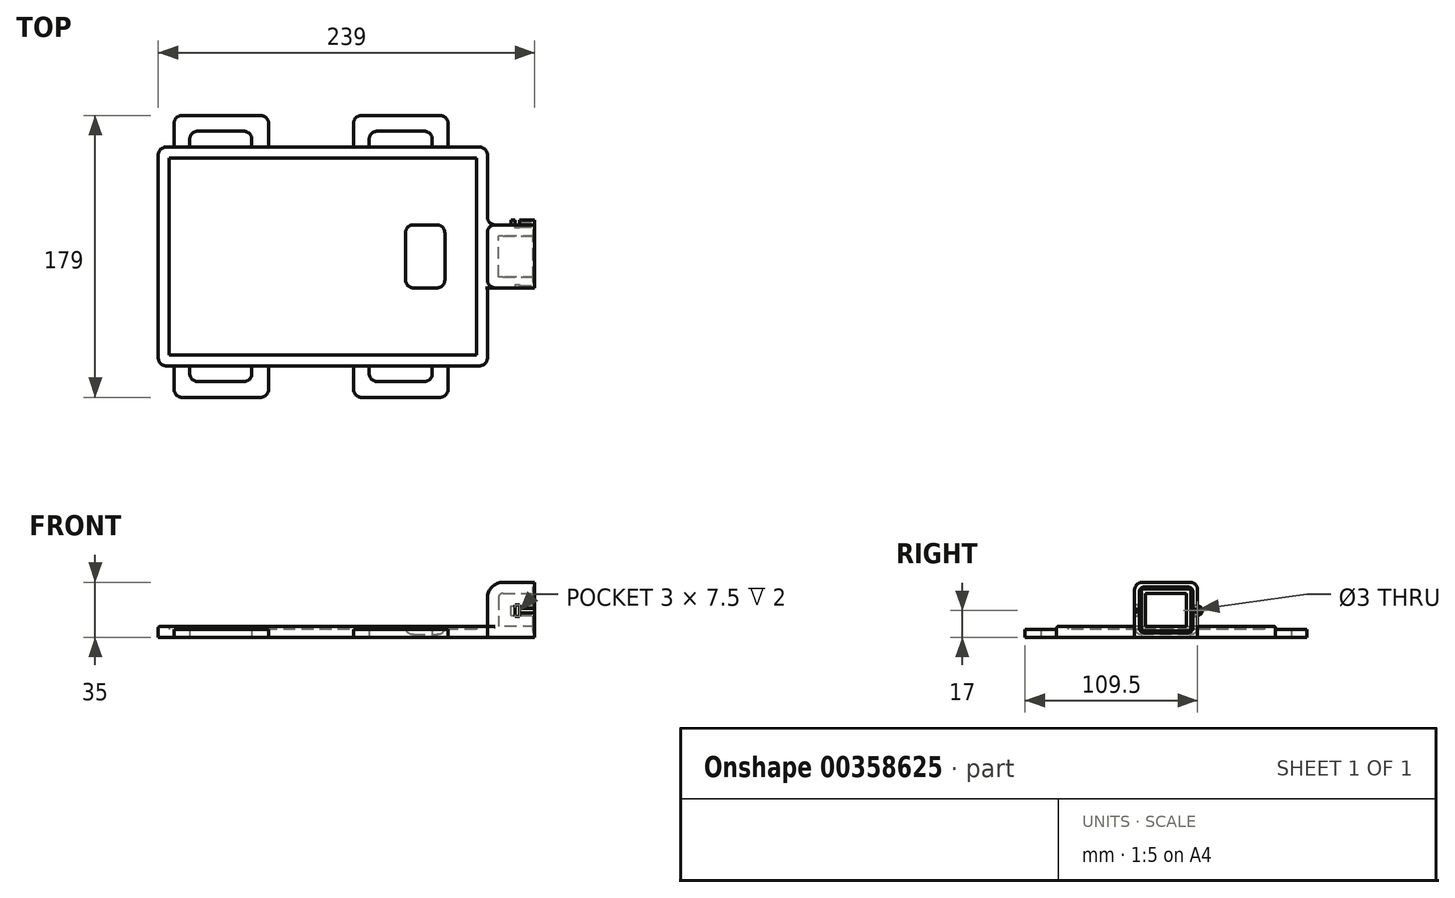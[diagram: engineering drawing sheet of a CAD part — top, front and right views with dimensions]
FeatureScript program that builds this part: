
annotation { "Feature Type Name" : "Feature", "Feature Type Description" : "" }
export const myFeature = defineFeature(function(context is Context, id is Id, definition is map)
    precondition{}
    {
        {
            var Q0;
            Q0=qCreatedBy(makeId("Top.planeOp"),FACE);
            var sketch = newSketch(context, id + "F0", { "sketchPlane" : qUnion([Q0])});
            skLineSegment(sketch, "E0.bottom", {"start": v(0, 0) * mm, "end": v(195, 0) * mm});
            skLineSegment(sketch, "E0.top", {"start": v(0, 125) * mm, "end": v(195, 125) * mm});
            skLineSegment(sketch, "E0.left", {"start": v(0, 0) * mm, "end": v(0, 125) * mm});
            skLineSegment(sketch, "E0.right", {"start": v(195, 0) * mm, "end": v(195, 125) * mm});
            skLineSegment(sketch, "E1.0", {"start": v(-7, 132) * mm, "end": v(202, 132) * mm});
            skLineSegment(sketch, "E1.1", {"start": v(-7, -7) * mm, "end": v(-7, 132) * mm});
            skLineSegment(sketch, "E1.2", {"start": v(-7, -7) * mm, "end": v(202, -7) * mm});
            skLineSegment(sketch, "E1.3", {"start": v(202, -7) * mm, "end": v(202, 132) * mm});
            skSolve(sketch);
        }
        {
            var Q0;
            Q0=makeQuery(id+"F0.imprint","IMPRINT",FACE,{"disambiguationData":[TD([[makeQuery(id+"F0.imprint","IMPRINT",EDGE,{"derivedFrom":sQuery(id+"F0.wireOp",EDGE,"E0.bottom")}),-1.0]])]});
            var Q1;
            Q1=makeQuery(id+"F0.imprint","IMPRINT",FACE,{"disambiguationData":[TD([[makeQuery(id+"F0.imprint","IMPRINT",EDGE,{"derivedFrom":sQuery(id+"F0.wireOp",EDGE,"E0.bottom")}),1.0]])]});
            extrude(context, id + "F1", {"entities" : qUnion([Q0, Q1]), "depth" : 5 * mm});
        }
        {
            var Q0;
            Q0 = qSketchRegion(id + "F0", true);
            extrude(context, id + "F2", {"entities" : qUnion([Q0]), "operationType" : NewBodyOperationType.ADD, "depth" : 7 * mm});
        }
        {
            var Q0;
            Q0=makeQuery(id+"F1.opExtrude","CAP_FACE",FACE,{"disambiguationData":[OSD([sQuery(id+"F0.wireOp",EDGE,"E1.0"),sQuery(id+"F0.wireOp",EDGE,"E1.1"),sQuery(id+"F0.wireOp",EDGE,"E1.2"),sQuery(id+"F0.wireOp",EDGE,"E1.3")])],"isStart":false});
            var sketch = newSketch(context, id + "F3", { "sketchPlane" : qUnion([Q0])});
            skLineSegment(sketch, "E2.bottom", {"start": v(150, 82.5) * mm, "end": v(175, 82.5) * mm});
            skLineSegment(sketch, "E2.top", {"start": v(150, 42.5) * mm, "end": v(175, 42.5) * mm});
            skLineSegment(sketch, "E2.left", {"start": v(150, 82.5) * mm, "end": v(150, 42.5) * mm});
            skLineSegment(sketch, "E2.right", {"start": v(175, 82.5) * mm, "end": v(175, 42.5) * mm});
            skSolve(sketch);
        }
        {
            var Q0;
            Q0=makeQuery(id+"F3.imprint","IMPRINT",FACE,{"disambiguationData":[TD([[makeQuery(id+"F3.imprint","IMPRINT",EDGE,{"derivedFrom":sQuery(id+"F3.wireOp",EDGE,"E2.bottom")}),-1.0]])]});
            extrude(context, id + "F4", {"entities" : qUnion([Q0]), "operationType" : NewBodyOperationType.REMOVE, "oppositeDirection" : true, "depth" : 3 * mm});
        }
        {
            var Q0;
            Q0=makeQuery(id+"F4.boolean.opBoolean","COPY",EDGE,{"derivedFrom":makeQuery(id+"F4.opExtrude","SWEPT_EDGE",EDGE,{"disambiguationData":[OSD([sQuery(id+"F3.wireOp",EDGE,"E2.top"),sQuery(id+"F3.wireOp",EDGE,"E2.left")])]})});
            var Q1;
            Q1=makeQuery(id+"F4.boolean.opBoolean","COPY",EDGE,{"derivedFrom":makeQuery(id+"F4.opExtrude","SWEPT_EDGE",EDGE,{"disambiguationData":[OSD([sQuery(id+"F3.wireOp",EDGE,"E2.bottom"),sQuery(id+"F3.wireOp",EDGE,"E2.left")])]})});
            var Q2;
            Q2=makeQuery(id+"F4.boolean.opBoolean","COPY",EDGE,{"derivedFrom":makeQuery(id+"F4.opExtrude","SWEPT_EDGE",EDGE,{"disambiguationData":[OSD([sQuery(id+"F3.wireOp",EDGE,"E2.bottom"),sQuery(id+"F3.wireOp",EDGE,"E2.right")])]})});
            var Q3;
            Q3=makeQuery(id+"F4.boolean.opBoolean","COPY",EDGE,{"derivedFrom":makeQuery(id+"F4.opExtrude","SWEPT_EDGE",EDGE,{"disambiguationData":[OSD([sQuery(id+"F3.wireOp",EDGE,"E2.top"),sQuery(id+"F3.wireOp",EDGE,"E2.right")])]})});
            fillet(context, id + "F5", {"entities" : qUnion([Q0, Q1, Q2, Q3]), "radius" : 5 * mm, "tangentPropagation" : true, "allowEdgeOverflow" : false});
        }
        {
            var Q0;
            Q0=makeQuery(id+"F4.boolean.opBoolean","COPY",FACE,{"derivedFrom":makeQuery(id+"F4.opExtrude","CAP_FACE",FACE,{"disambiguationData":[OSD([sQuery(id+"F3.wireOp",EDGE,"E2.bottom"),sQuery(id+"F3.wireOp",EDGE,"E2.top"),sQuery(id+"F3.wireOp",EDGE,"E2.left"),sQuery(id+"F3.wireOp",EDGE,"E2.right")])],"isStart":false})});
            fillet(context, id + "F6", {"entities" : qUnion([Q0]), "radius" : 5 * mm, "tangentPropagation" : true, "allowEdgeOverflow" : false});
        }
        {
            var Q0;
            {var subQ0=sQuery(id+"F0.wireOp",EDGE,"E1.3");Q0=makeQuery(id+"F2.boolean.opBoolean","MERGE",FACE,{"derivedFrom":[makeQuery(id+"F1.opExtrude","SWEPT_FACE",FACE,{"disambiguationData":[OSD([subQ0])]}),makeQuery(id+"F2.opExtrude","SWEPT_FACE",FACE,{"disambiguationData":[OSD([subQ0])]})]});}
            var sketch = newSketch(context, id + "F7", { "sketchPlane" : qUnion([Q0])});
            skLineSegment(sketch, "E3.bottom", {"start": v(42.5, 0) * mm, "end": v(82.5, 0) * mm});
            skLineSegment(sketch, "E3.top", {"start": v(42.5, 35) * mm, "end": v(82.5, 35) * mm});
            skLineSegment(sketch, "E3.left", {"start": v(42.5, 0) * mm, "end": v(42.5, 35) * mm});
            skLineSegment(sketch, "E3.right", {"start": v(82.5, 0) * mm, "end": v(82.5, 35) * mm});
            skSolve(sketch);
        }
        {
            var Q0;
            {var subQ0=sQuery(id+"F7.wireOp",EDGE,"E3.top");Q0=makeQuery(id+"F7.imprint","IMPRINT",FACE,{"disambiguationData":[TD([[makeQuery(id+"F7.imprint","IMPRINT",EDGE,{"derivedFrom":subQ0}),-1.0]])]});}
            var Q1;
            {var subQ0=sQuery(id+"F7.wireOp",EDGE,"E3.bottom");Q1=makeQuery(id+"F7.imprint","IMPRINT",FACE,{"disambiguationData":[TD([[makeQuery(id+"F7.imprint","IMPRINT",EDGE,{"derivedFrom":subQ0}),1.0]])]});}
            extrude(context, id + "F8", {"entities" : qUnion([Q0, Q1]), "operationType" : NewBodyOperationType.ADD, "depth" : 30 * mm});
        }
        {
            var Q0;
            Q0=makeQuery(id+"F8.opExtrude","CAP_EDGE",EDGE,{"disambiguationData":[OSD([sQuery(id+"F7.wireOp",EDGE,"E3.top")])],"isStart":true});
            fillet(context, id + "F9", {"entities" : qUnion([Q0]), "radius" : 10 * mm, "tangentPropagation" : true, "allowEdgeOverflow" : false});
        }
        {
            var Q0;
            Q0=makeQuery(id+"F8.opExtrude","SWEPT_EDGE",EDGE,{"disambiguationData":[OSD([sQuery(id+"F7.wireOp",EDGE,"E3.top"),sQuery(id+"F7.wireOp",EDGE,"E3.left")])]});
            var Q1;
            Q1=makeQuery(id+"F8.opExtrude","SWEPT_EDGE",EDGE,{"disambiguationData":[OSD([sQuery(id+"F7.wireOp",EDGE,"E3.top"),sQuery(id+"F7.wireOp",EDGE,"E3.right")])]});
            fillet(context, id + "F10", {"entities" : qUnion([Q0, Q1]), "radius" : 5 * mm, "tangentPropagation" : true, "allowEdgeOverflow" : false});
        }
        {
            var Q0;
            {var subQ0=sQuery(id+"F0.wireOp",EDGE,"E1.3");var subQ1=sQuery(id+"F7.wireOp",EDGE,"E3.left");Q0=makeQuery(id+"F8.boolean.opBoolean","SPLIT",EDGE,{"disambiguationData":[topologyDisambiguationEdgeConnected([makeQuery(id+"F1.opExtrude","SWEPT_FACE",FACE,{"disambiguationData":[OSD([subQ0])]})])],"derivedFrom":makeQuery(id+"F8.opExtrude","CAP_EDGE",EDGE,{"disambiguationData":[OSD([subQ1])],"isStart":true})});}
            var Q1;
            {var subQ0=sQuery(id+"F0.wireOp",EDGE,"E1.3");var subQ1=sQuery(id+"F7.wireOp",EDGE,"E3.right");Q1=makeQuery(id+"F8.boolean.opBoolean","SPLIT",EDGE,{"disambiguationData":[topologyDisambiguationEdgeConnected([makeQuery(id+"F1.opExtrude","SWEPT_FACE",FACE,{"disambiguationData":[OSD([subQ0])]})])],"derivedFrom":makeQuery(id+"F8.opExtrude","CAP_EDGE",EDGE,{"disambiguationData":[OSD([subQ1])],"isStart":true})});}
            fillet(context, id + "F11", {"entities" : qUnion([Q0, Q1]), "radius" : 5 * mm, "tangentPropagation" : true, "allowEdgeOverflow" : false});
        }
        {
            var Q0;
            Q0=makeQuery(id+"F8.opExtrude","CAP_FACE",FACE,{"disambiguationData":[OSD([sQuery(id+"F7.wireOp",EDGE,"E3.bottom"),sQuery(id+"F7.wireOp",EDGE,"E3.top"),sQuery(id+"F7.wireOp",EDGE,"E3.left"),sQuery(id+"F7.wireOp",EDGE,"E3.right")])],"isStart":false});
            shell(context, id + "F12", {"entities" : qUnion([Q0]), "thickness" : 7 * mm});
        }
        {
            var Q0;
            Q0=makeQuery(id+"F8.opExtrude","CAP_FACE",FACE,{"disambiguationData":[OSD([sQuery(id+"F7.wireOp",EDGE,"E3.bottom"),sQuery(id+"F7.wireOp",EDGE,"E3.top"),sQuery(id+"F7.wireOp",EDGE,"E3.left"),sQuery(id+"F7.wireOp",EDGE,"E3.right")])],"isStart":false});
            var sketch = newSketch(context, id + "F13", { "sketchPlane" : qUnion([Q0])});
            skPoint(sketch, "E4.0", {"position": v(43.96, 33.54) * mm});
            skPoint(sketch, "E5.0", {"position": v(81.04, 33.54) * mm});
            skLineSegment(sketch, "E6.0", {"start": v(48.5, 32) * mm, "end": v(76.5, 32) * mm});
            skLineSegment(sketch, "E6.1", {"start": v(45.5, 6) * mm, "end": v(45.5, 29) * mm});
            skLineSegment(sketch, "E6.2", {"start": v(48.5, 3) * mm, "end": v(76.5, 3) * mm});
            skLineSegment(sketch, "E6.3", {"start": v(79.5, 6) * mm, "end": v(79.5, 29) * mm});
            skPoint(sketch, "E7.visualSharp", {"position": v(45.5, 32) * mm});
            skArc(sketch, "E7.filletArc", {"start": v(48.5, 32) * mm, "mid": v(46.38, 31.12) * mm, "end": v(45.5, 29) * mm});
            skPoint(sketch, "E8.visualSharp", {"position": v(79.5, 32) * mm});
            skArc(sketch, "E8.filletArc", {"start": v(79.5, 29) * mm, "mid": v(78.62, 31.12) * mm, "end": v(76.5, 32) * mm});
            skPoint(sketch, "E9.visualSharp", {"position": v(79.5, 3) * mm});
            skArc(sketch, "E9.filletArc", {"start": v(76.5, 3) * mm, "mid": v(78.62, 3.88) * mm, "end": v(79.5, 6) * mm});
            skPoint(sketch, "E10.visualSharp", {"position": v(45.5, 3) * mm});
            skArc(sketch, "E10.filletArc", {"start": v(45.5, 6) * mm, "mid": v(46.38, 3.88) * mm, "end": v(48.5, 3) * mm});
            skLineSegment(sketch, "E11.0", {"start": v(54.5, 23) * mm, "end": v(70.5, 23) * mm});
            skLineSegment(sketch, "E11.1", {"start": v(54.5, 12) * mm, "end": v(54.5, 23) * mm});
            skLineSegment(sketch, "E11.2", {"start": v(54.5, 12) * mm, "end": v(70.5, 12) * mm});
            skLineSegment(sketch, "E11.3", {"start": v(70.5, 12) * mm, "end": v(70.5, 23) * mm});
            skLineSegment(sketch, "E12.0", {"start": v(48.7, 30.8) * mm, "end": v(76.3, 30.8) * mm});
            skLineSegment(sketch, "E12.1", {"start": v(46.7, 6.2) * mm, "end": v(46.7, 28.8) * mm});
            skLineSegment(sketch, "E12.2", {"start": v(48.7, 4.2) * mm, "end": v(76.3, 4.2) * mm});
            skLineSegment(sketch, "E12.3", {"start": v(78.3, 6.2) * mm, "end": v(78.3, 28.8) * mm});
            skPoint(sketch, "E13.visualSharp", {"position": v(46.7, 30.8) * mm});
            skArc(sketch, "E13.filletArc", {"start": v(48.7, 30.8) * mm, "mid": v(47.29, 30.21) * mm, "end": v(46.7, 28.8) * mm});
            skPoint(sketch, "E14.visualSharp", {"position": v(78.3, 30.8) * mm});
            skArc(sketch, "E14.filletArc", {"start": v(78.3, 28.8) * mm, "mid": v(77.71, 30.21) * mm, "end": v(76.3, 30.8) * mm});
            skPoint(sketch, "E15.visualSharp", {"position": v(78.3, 4.2) * mm});
            skArc(sketch, "E15.filletArc", {"start": v(76.3, 4.2) * mm, "mid": v(77.71, 4.79) * mm, "end": v(78.3, 6.2) * mm});
            skPoint(sketch, "E16.visualSharp", {"position": v(46.7, 4.2) * mm});
            skArc(sketch, "E16.filletArc", {"start": v(46.7, 6.2) * mm, "mid": v(47.29, 4.79) * mm, "end": v(48.7, 4.2) * mm});
            skPoint(sketch, "E17.orphan", {"position": v(47.5, 35) * mm});
            skPoint(sketch, "E18.0.end.orphan", {"position": v(42.5, 30) * mm});
            skPoint(sketch, "E19.0.start.orphan", {"position": v(42.5, 0) * mm});
            skPoint(sketch, "E20.0.start.orphan", {"position": v(82.5, 0) * mm});
            skPoint(sketch, "E21.orphan", {"position": v(82.5, 30) * mm});
            skPoint(sketch, "E22.0.end.orphan", {"position": v(77.5, 35) * mm});
            skSolve(sketch);
        }
        {
            var Q0;
            Q0=makeQuery(id+"F13.imprint","IMPRINT",FACE,{"disambiguationData":[TD([[makeQuery(id+"F13.imprint","IMPRINT",EDGE,{"derivedFrom":sQuery(id+"F13.wireOp",EDGE,"E6.0")}),-1.0]])]});
            extrude(context, id + "F14", {"entities" : qUnion([Q0]), "operationType" : NewBodyOperationType.REMOVE, "oppositeDirection" : true, "depth" : 1 * mm});
        }
        {
            var Q0;
            {var subQ0=sQuery(id+"F7.wireOp",EDGE,"E3.right");var subQ1=sQuery(id+"F7.wireOp",EDGE,"E3.top");var subQ2=sQuery(id+"F7.wireOp",EDGE,"E3.left");var subQ3=sQuery(id+"F7.wireOp",EDGE,"E3.bottom");Q0=makeQuery(id+"F14.boolean.opBoolean","SPLIT",FACE,{"disambiguationData":[TD([makeQuery(id+"F8.opExtrude","SWEPT_FACE",FACE,{"disambiguationData":[OSD([subQ3])]})])],"derivedFrom":makeQuery(id+"F8.opExtrude","CAP_FACE",FACE,{"disambiguationData":[OSD([subQ3,subQ1,subQ2,subQ0])],"isStart":false})});}
            var sketch = newSketch(context, id + "F15", { "sketchPlane" : qUnion([Q0])});
            skCircle(sketch, "E23", {"center": v(42.5, 17) * mm, "radius": 3 * mm});
            skCircle(sketch, "E24", {"center": v(42.5, 17) * mm, "radius": 1.5 * mm});
            skCircle(sketch, "E25", {"center": v(82.5, 17) * mm, "radius": 3 * mm});
            skCircle(sketch, "E26", {"center": v(82.5, 17) * mm, "radius": 1.5 * mm});
            skSolve(sketch);
        }
        {
            var Q0;
            {var subQ0=sQuery(id+"F15.wireOp",EDGE,"E23");var subQ1=makeQuery(id+"F8.opExtrude","CAP_EDGE",EDGE,{"disambiguationData":[OSD([sQuery(id+"F7.wireOp",EDGE,"E3.left")])],"isStart":false});var subQ2=makeQuery(id+"F15.imprint","INTERSECT",VERTEX,{"disambiguationData":[OD(0.0)],"derivedFrom":[subQ1,subQ0]});Q0=makeQuery(id+"F15.imprint","IMPRINT",FACE,{"disambiguationData":[TD([[makeQuery(id+"F15.imprint","IMPRINT",EDGE,{"disambiguationData":[TD([[subQ2,-1.0]])],"derivedFrom":subQ0}),1.0]])]});}
            var Q1;
            {var subQ0=sQuery(id+"F15.wireOp",EDGE,"E25");var subQ1=makeQuery(id+"F8.opExtrude","CAP_EDGE",EDGE,{"disambiguationData":[OSD([sQuery(id+"F7.wireOp",EDGE,"E3.right")])],"isStart":false});var subQ2=makeQuery(id+"F15.imprint","INTERSECT",VERTEX,{"disambiguationData":[OD(0.0)],"derivedFrom":[subQ1,subQ0]});Q1=makeQuery(id+"F15.imprint","IMPRINT",FACE,{"disambiguationData":[TD([[makeQuery(id+"F15.imprint","IMPRINT",EDGE,{"disambiguationData":[TD([[subQ2,1.0]])],"derivedFrom":subQ0}),1.0]])]});}
            var Q2;
            {var subQ0=sQuery(id+"F15.wireOp",EDGE,"E26");var subQ1=makeQuery(id+"F8.opExtrude","CAP_EDGE",EDGE,{"disambiguationData":[OSD([sQuery(id+"F7.wireOp",EDGE,"E3.right")])],"isStart":false});var subQ2=makeQuery(id+"F15.imprint","INTERSECT",VERTEX,{"disambiguationData":[OD(0.0)],"derivedFrom":[subQ1,subQ0]});Q2=makeQuery(id+"F15.imprint","IMPRINT",FACE,{"disambiguationData":[TD([[makeQuery(id+"F15.imprint","IMPRINT",EDGE,{"disambiguationData":[TD([[subQ2,1.0]])],"derivedFrom":subQ0}),1.0]])]});}
            var Q3;
            {var subQ0=sQuery(id+"F15.wireOp",EDGE,"E24");var subQ1=makeQuery(id+"F8.opExtrude","CAP_EDGE",EDGE,{"disambiguationData":[OSD([sQuery(id+"F7.wireOp",EDGE,"E3.left")])],"isStart":false});var subQ2=makeQuery(id+"F15.imprint","INTERSECT",VERTEX,{"disambiguationData":[OD(0.0)],"derivedFrom":[subQ1,subQ0]});Q3=makeQuery(id+"F15.imprint","IMPRINT",FACE,{"disambiguationData":[TD([[makeQuery(id+"F15.imprint","IMPRINT",EDGE,{"disambiguationData":[TD([[subQ2,-1.0]])],"derivedFrom":subQ0}),1.0]])]});}
            extrude(context, id + "F16", {"entities" : qUnion([Q0, Q1, Q2, Q3]), "operationType" : NewBodyOperationType.ADD, "oppositeDirection" : true, "depth" : 15 * mm});
        }
        {
            var Q0;
            {var subQ0=sQuery(id+"F15.wireOp",EDGE,"E26");var subQ1=makeQuery(id+"F8.opExtrude","CAP_EDGE",EDGE,{"disambiguationData":[OSD([sQuery(id+"F7.wireOp",EDGE,"E3.right")])],"isStart":false});var subQ2=makeQuery(id+"F15.imprint","INTERSECT",VERTEX,{"disambiguationData":[OD(0.0)],"derivedFrom":[subQ1,subQ0]});Q0=makeQuery(id+"F15.imprint","IMPRINT",FACE,{"disambiguationData":[TD([[makeQuery(id+"F15.imprint","IMPRINT",EDGE,{"disambiguationData":[TD([[subQ2,-1.0]])],"derivedFrom":subQ0}),1.0]])]});}
            var Q1;
            {var subQ0=sQuery(id+"F15.wireOp",EDGE,"E26");var subQ1=makeQuery(id+"F8.opExtrude","CAP_EDGE",EDGE,{"disambiguationData":[OSD([sQuery(id+"F7.wireOp",EDGE,"E3.right")])],"isStart":false});var subQ2=makeQuery(id+"F15.imprint","INTERSECT",VERTEX,{"disambiguationData":[OD(0.0)],"derivedFrom":[subQ1,subQ0]});Q1=makeQuery(id+"F15.imprint","IMPRINT",FACE,{"disambiguationData":[TD([[makeQuery(id+"F15.imprint","IMPRINT",EDGE,{"disambiguationData":[TD([[subQ2,1.0]])],"derivedFrom":subQ0}),1.0]])]});}
            var Q2;
            {var subQ0=sQuery(id+"F15.wireOp",EDGE,"E24");var subQ1=makeQuery(id+"F8.opExtrude","CAP_EDGE",EDGE,{"disambiguationData":[OSD([sQuery(id+"F7.wireOp",EDGE,"E3.left")])],"isStart":false});var subQ2=makeQuery(id+"F15.imprint","INTERSECT",VERTEX,{"disambiguationData":[OD(0.0)],"derivedFrom":[subQ1,subQ0]});Q2=makeQuery(id+"F15.imprint","IMPRINT",FACE,{"disambiguationData":[TD([[makeQuery(id+"F15.imprint","IMPRINT",EDGE,{"disambiguationData":[TD([[subQ2,-1.0]])],"derivedFrom":subQ0}),1.0]])]});}
            var Q3;
            {var subQ0=sQuery(id+"F15.wireOp",EDGE,"E24");var subQ1=makeQuery(id+"F8.opExtrude","CAP_EDGE",EDGE,{"disambiguationData":[OSD([sQuery(id+"F7.wireOp",EDGE,"E3.left")])],"isStart":false});var subQ2=makeQuery(id+"F15.imprint","INTERSECT",VERTEX,{"disambiguationData":[OD(0.0)],"derivedFrom":[subQ1,subQ0]});Q3=makeQuery(id+"F15.imprint","IMPRINT",FACE,{"disambiguationData":[TD([[makeQuery(id+"F15.imprint","IMPRINT",EDGE,{"disambiguationData":[TD([[subQ2,1.0]])],"derivedFrom":subQ0}),1.0]])]});}
            extrude(context, id + "F17", {"entities" : qUnion([Q0, Q1, Q2, Q3]), "operationType" : NewBodyOperationType.REMOVE, "oppositeDirection" : true, "depth" : 10 * mm});
        }
        {
            var Q0;
            Q0=makeQuery(id+"F8.opExtrude","SWEPT_FACE",FACE,{"disambiguationData":[OSD([sQuery(id+"F7.wireOp",EDGE,"E3.left")])]});
            var sketch = newSketch(context, id + "F18", { "sketchPlane" : qUnion([Q0])});
            skLineSegment(sketch, "E27.bottom", {"start": v(219.5, 20.7) * mm, "end": v(222.5, 20.7) * mm});
            skLineSegment(sketch, "E27.top", {"start": v(219.5, 13.2) * mm, "end": v(222.5, 13.2) * mm});
            skLineSegment(sketch, "E27.left", {"start": v(219.5, 20.7) * mm, "end": v(219.5, 13.2) * mm});
            skLineSegment(sketch, "E27.right", {"start": v(222.5, 20.7) * mm, "end": v(222.5, 13.2) * mm});
            skSolve(sketch);
        }
        {
            var Q0;
            Q0 = qSketchRegion(id + "F18", true);
            extrude(context, id + "F19", {"entities" : qUnion([Q0]), "operationType" : NewBodyOperationType.REMOVE, "oppositeDirection" : true, "depth" : 2 * mm, "hasSecondDirection" : true, "secondDirectionOppositeDirection" : false, "secondDirectionDepth" : 25 * mm});
        }
        {
            var Q0;
            Q0=makeQuery(id+"F8.opExtrude","SWEPT_FACE",FACE,{"disambiguationData":[OSD([sQuery(id+"F7.wireOp",EDGE,"E3.right")])]});
            var sketch = newSketch(context, id + "F20", { "sketchPlane" : qUnion([Q0])});
            skLineSegment(sketch, "E28.bottom", {"start": v(-222.5, 20.7) * mm, "end": v(-219.5, 20.7) * mm});
            skLineSegment(sketch, "E28.top", {"start": v(-222.5, 13.2) * mm, "end": v(-219.5, 13.2) * mm});
            skLineSegment(sketch, "E28.left", {"start": v(-222.5, 20.7) * mm, "end": v(-222.5, 13.2) * mm});
            skLineSegment(sketch, "E28.right", {"start": v(-219.5, 20.7) * mm, "end": v(-219.5, 13.2) * mm});
            skSolve(sketch);
        }
        {
            var Q0;
            Q0 = qSketchRegion(id + "F20", true);
            extrude(context, id + "F21", {"entities" : qUnion([Q0]), "operationType" : NewBodyOperationType.REMOVE, "oppositeDirection" : true, "depth" : 2 * mm, "hasSecondDirection" : true, "secondDirectionOppositeDirection" : false, "secondDirectionDepth" : 25 * mm});
        }
        {
            var Q0;
            {var subQ0=sQuery(id+"F0.wireOp",EDGE,"E1.3");var subQ1=sQuery(id+"F0.wireOp",EDGE,"E1.0");Q0=makeQuery(id+"F2.boolean.opBoolean","MERGE",EDGE,{"derivedFrom":[makeQuery(id+"F1.opExtrude","SWEPT_EDGE",EDGE,{"disambiguationData":[OSD([subQ1,subQ0])]}),makeQuery(id+"F2.opExtrude","SWEPT_EDGE",EDGE,{"disambiguationData":[OSD([subQ1,subQ0])]})]});}
            var Q1;
            {var subQ0=sQuery(id+"F0.wireOp",EDGE,"E1.1");var subQ1=sQuery(id+"F0.wireOp",EDGE,"E1.0");Q1=makeQuery(id+"F2.boolean.opBoolean","MERGE",EDGE,{"derivedFrom":[makeQuery(id+"F1.opExtrude","SWEPT_EDGE",EDGE,{"disambiguationData":[OSD([subQ1,subQ0])]}),makeQuery(id+"F2.opExtrude","SWEPT_EDGE",EDGE,{"disambiguationData":[OSD([subQ1,subQ0])]})]});}
            var Q2;
            {var subQ0=sQuery(id+"F0.wireOp",EDGE,"E1.2");var subQ1=sQuery(id+"F0.wireOp",EDGE,"E1.1");Q2=makeQuery(id+"F2.boolean.opBoolean","MERGE",EDGE,{"derivedFrom":[makeQuery(id+"F1.opExtrude","SWEPT_EDGE",EDGE,{"disambiguationData":[OSD([subQ1,subQ0])]}),makeQuery(id+"F2.opExtrude","SWEPT_EDGE",EDGE,{"disambiguationData":[OSD([subQ1,subQ0])]})]});}
            var Q3;
            {var subQ0=sQuery(id+"F0.wireOp",EDGE,"E1.3");var subQ1=sQuery(id+"F0.wireOp",EDGE,"E1.2");Q3=makeQuery(id+"F2.boolean.opBoolean","MERGE",EDGE,{"derivedFrom":[makeQuery(id+"F1.opExtrude","SWEPT_EDGE",EDGE,{"disambiguationData":[OSD([subQ1,subQ0])]}),makeQuery(id+"F2.opExtrude","SWEPT_EDGE",EDGE,{"disambiguationData":[OSD([subQ1,subQ0])]})]});}
            fillet(context, id + "F22", {"entities" : qUnion([Q0, Q1, Q2, Q3]), "radius" : 5 * mm, "tangentPropagation" : true, "allowEdgeOverflow" : false});
        }
        {
            var Q0;
            {var subQ0=sQuery(id+"F0.wireOp",EDGE,"E1.3");var subQ1=sQuery(id+"F0.wireOp",EDGE,"E1.2");Q0=makeQuery(id+"F22.opFillet","BLEND_EDGE",EDGE,{"blendedFrom":[makeQuery(id+"F2.boolean.opBoolean","MERGE",EDGE,{"derivedFrom":[makeQuery(id+"F1.opExtrude","SWEPT_EDGE",EDGE,{"disambiguationData":[OSD([subQ1,subQ0])]}),makeQuery(id+"F2.opExtrude","SWEPT_EDGE",EDGE,{"disambiguationData":[OSD([subQ1,subQ0])]})]}),makeQuery(id+"F2.opExtrude","CAP_FACE",FACE,{"disambiguationData":[OSD([sQuery(id+"F0.wireOp",EDGE,"E0.bottom"),sQuery(id+"F0.wireOp",EDGE,"E0.top"),sQuery(id+"F0.wireOp",EDGE,"E0.left"),sQuery(id+"F0.wireOp",EDGE,"E0.right"),sQuery(id+"F0.wireOp",EDGE,"E1.0"),sQuery(id+"F0.wireOp",EDGE,"E1.1"),subQ1,subQ0])],"isStart":false})],"blendedInto":[makeQuery(id+"F2.opExtrude","CAP_FACE",FACE,{"disambiguationData":[OSD([sQuery(id+"F0.wireOp",EDGE,"E0.bottom"),sQuery(id+"F0.wireOp",EDGE,"E0.top"),sQuery(id+"F0.wireOp",EDGE,"E0.left"),sQuery(id+"F0.wireOp",EDGE,"E0.right"),sQuery(id+"F0.wireOp",EDGE,"E1.0"),sQuery(id+"F0.wireOp",EDGE,"E1.1"),subQ1,subQ0])],"isStart":false})]});}
            fillet(context, id + "F23", {"entities" : qUnion([Q0]), "radius" : 1 * mm, "tangentPropagation" : true, "allowEdgeOverflow" : false});
        }
        {
            var Q0;
            Q0=makeQuery(id+"F8.boolean.opBoolean","MERGE",FACE,{"derivedFrom":[makeQuery(id+"F1.opExtrude","CAP_FACE",FACE,{"disambiguationData":[OSD([sQuery(id+"F0.wireOp",EDGE,"E1.0"),sQuery(id+"F0.wireOp",EDGE,"E1.1"),sQuery(id+"F0.wireOp",EDGE,"E1.2"),sQuery(id+"F0.wireOp",EDGE,"E1.3")])],"isStart":true}),makeQuery(id+"F8.opExtrude","SWEPT_FACE",FACE,{"disambiguationData":[OSD([sQuery(id+"F7.wireOp",EDGE,"E3.bottom")])]})]});
            var sketch = newSketch(context, id + "F24", { "sketchPlane" : qUnion([Q0])});
            skLineSegment(sketch, "E29.bottom", {"start": v(167, 7) * mm, "end": v(127, 7) * mm});
            skLineSegment(sketch, "E30.bottom", {"start": v(117, 7) * mm, "end": v(177, 7) * mm});
            skLineSegment(sketch, "E30.top", {"start": v(117, 27) * mm, "end": v(177, 27) * mm});
            skLineSegment(sketch, "E30.left", {"start": v(117, 7) * mm, "end": v(117, 27) * mm});
            skLineSegment(sketch, "E30.right", {"start": v(177, 7) * mm, "end": v(177, 27) * mm});
            skLineSegment(sketch, "E31.bottom", {"start": v(127, 7) * mm, "end": v(167, 7) * mm});
            skLineSegment(sketch, "E31.top", {"start": v(127, 17) * mm, "end": v(167, 17) * mm});
            skLineSegment(sketch, "E31.left", {"start": v(127, 7) * mm, "end": v(127, 17) * mm});
            skLineSegment(sketch, "E31.right", {"start": v(167, 7) * mm, "end": v(167, 17) * mm});
            skLineSegment(sketch, "E32.bottom", {"start": v(52.4, 7) * mm, "end": v(13, 7) * mm});
            skLineSegment(sketch, "E33.bottom", {"start": v(3, 7) * mm, "end": v(63, 7) * mm});
            skLineSegment(sketch, "E33.top", {"start": v(3, 27) * mm, "end": v(63, 27) * mm});
            skLineSegment(sketch, "E33.left", {"start": v(3, 7) * mm, "end": v(3, 27) * mm});
            skLineSegment(sketch, "E33.right", {"start": v(63, 7) * mm, "end": v(63, 27) * mm});
            skLineSegment(sketch, "E34.bottom", {"start": v(13, 7) * mm, "end": v(52.4, 7) * mm});
            skLineSegment(sketch, "E34.top", {"start": v(13, 17) * mm, "end": v(52.4, 17) * mm});
            skLineSegment(sketch, "E34.left", {"start": v(13, 7) * mm, "end": v(13, 17) * mm});
            skLineSegment(sketch, "E34.right", {"start": v(52.4, 7) * mm, "end": v(52.4, 17) * mm});
            skLineSegment(sketch, "E35", {"start": v(-7, -62.5) * mm, "end": v(232, -62.5) * mm});
            skLineSegment(sketch, "E36.MirrorCS", {"start": v(3, -132) * mm, "end": v(3, -152) * mm});
            skLineSegment(sketch, "E37.MirrorCS", {"start": v(3, -152) * mm, "end": v(63, -152) * mm});
            skLineSegment(sketch, "E38.MirrorCS", {"start": v(13, -142) * mm, "end": v(52.4, -142) * mm});
            skLineSegment(sketch, "E39.MirrorCS", {"start": v(13, -132) * mm, "end": v(13, -142) * mm});
            skLineSegment(sketch, "E40.MirrorCS", {"start": v(52.4, -132) * mm, "end": v(52.4, -142) * mm});
            skLineSegment(sketch, "E41.MirrorCS", {"start": v(63, -132) * mm, "end": v(63, -152) * mm});
            skLineSegment(sketch, "E42.MirrorCS", {"start": v(117, -132) * mm, "end": v(117, -152) * mm});
            skLineSegment(sketch, "E43.MirrorCS", {"start": v(117, -152) * mm, "end": v(177, -152) * mm});
            skLineSegment(sketch, "E44.MirrorCS", {"start": v(127, -142) * mm, "end": v(167, -142) * mm});
            skLineSegment(sketch, "E45.MirrorCS", {"start": v(127, -132) * mm, "end": v(127, -142) * mm});
            skLineSegment(sketch, "E46.MirrorCS", {"start": v(167, -132) * mm, "end": v(167, -142) * mm});
            skLineSegment(sketch, "E47.MirrorCS", {"start": v(177, -132) * mm, "end": v(177, -152) * mm});
            skSolve(sketch);
        }
        {
            var Q0;
            Q0=makeQuery(id+"F24.imprint","IMPRINT",FACE,{"disambiguationData":[TD([[makeQuery(id+"F24.imprint","IMPRINT",EDGE,{"derivedFrom":sQuery(id+"F24.wireOp",EDGE,"E30.top")}),-1.0]])]});
            var Q1;
            Q1=makeQuery(id+"F24.imprint","IMPRINT",FACE,{"disambiguationData":[TD([[makeQuery(id+"F24.imprint","IMPRINT",EDGE,{"derivedFrom":sQuery(id+"F24.wireOp",EDGE,"E33.top")}),-1.0]])]});
            var Q2;
            {var subQ1=sQuery(id+"F24.wireOp",EDGE,"E36.MirrorCS");Q2=makeQuery(id+"F24.imprint","IMPRINT",FACE,{"disambiguationData":[TD([[makeQuery(id+"F24.imprint","IMPRINT",EDGE,{"derivedFrom":subQ1}),1.0]])]});}
            var Q3;
            {var subQ1=sQuery(id+"F24.wireOp",EDGE,"E42.MirrorCS");Q3=makeQuery(id+"F24.imprint","IMPRINT",FACE,{"disambiguationData":[TD([[makeQuery(id+"F24.imprint","IMPRINT",EDGE,{"derivedFrom":subQ1}),1.0]])]});}
            extrude(context, id + "F25", {"entities" : qUnion([Q0, Q1, Q2, Q3]), "operationType" : NewBodyOperationType.ADD, "oppositeDirection" : true, "depth" : 5 * mm});
        }
        {
            var Q0;
            Q0=makeQuery(id+"F25.opExtrude","SWEPT_EDGE",EDGE,{"disambiguationData":[OSD([sQuery(id+"F24.wireOp",EDGE,"E33.top"),sQuery(id+"F24.wireOp",EDGE,"E33.right")])]});
            var Q1;
            Q1=makeQuery(id+"F25.opExtrude","SWEPT_EDGE",EDGE,{"disambiguationData":[OSD([sQuery(id+"F24.wireOp",EDGE,"E30.top"),sQuery(id+"F24.wireOp",EDGE,"E30.left")])]});
            var Q2;
            Q2=makeQuery(id+"F25.opExtrude","SWEPT_EDGE",EDGE,{"disambiguationData":[OSD([sQuery(id+"F24.wireOp",EDGE,"E30.top"),sQuery(id+"F24.wireOp",EDGE,"E30.right")])]});
            var Q3;
            Q3=makeQuery(id+"F25.opExtrude","SWEPT_EDGE",EDGE,{"disambiguationData":[OSD([sQuery(id+"F24.wireOp",EDGE,"E33.top"),sQuery(id+"F24.wireOp",EDGE,"E33.left")])]});
            var Q4;
            Q4=makeQuery(id+"F25.opExtrude","SWEPT_EDGE",EDGE,{"disambiguationData":[OSD([sQuery(id+"F0.wireOp",EDGE,"E1.2"),sQuery(id+"F24.wireOp",EDGE,"E33.bottom"),sQuery(id+"F24.wireOp",EDGE,"E33.left")])]});
            var Q5;
            Q5=makeQuery(id+"F25.opExtrude","SWEPT_EDGE",EDGE,{"disambiguationData":[OSD([sQuery(id+"F0.wireOp",EDGE,"E1.2"),sQuery(id+"F24.wireOp",EDGE,"E33.bottom"),sQuery(id+"F24.wireOp",EDGE,"E33.right")])]});
            var Q6;
            Q6=makeQuery(id+"F25.opExtrude","SWEPT_EDGE",EDGE,{"disambiguationData":[OSD([sQuery(id+"F0.wireOp",EDGE,"E1.2"),sQuery(id+"F24.wireOp",EDGE,"E30.bottom"),sQuery(id+"F24.wireOp",EDGE,"E30.left")])]});
            var Q7;
            Q7=makeQuery(id+"F25.opExtrude","SWEPT_EDGE",EDGE,{"disambiguationData":[OSD([sQuery(id+"F0.wireOp",EDGE,"E1.2"),sQuery(id+"F24.wireOp",EDGE,"E30.bottom"),sQuery(id+"F24.wireOp",EDGE,"E30.right")])]});
            var Q8;
            Q8=makeQuery(id+"F25.opExtrude","SWEPT_EDGE",EDGE,{"disambiguationData":[OSD([sQuery(id+"F24.wireOp",EDGE,"E43.MirrorCS"),sQuery(id+"F24.wireOp",EDGE,"E47.MirrorCS")])]});
            var Q9;
            Q9=makeQuery(id+"F25.opExtrude","SWEPT_EDGE",EDGE,{"disambiguationData":[OSD([sQuery(id+"F0.wireOp",EDGE,"E1.0"),sQuery(id+"F24.wireOp",EDGE,"E47.MirrorCS")])]});
            var Q10;
            Q10=makeQuery(id+"F25.opExtrude","SWEPT_EDGE",EDGE,{"disambiguationData":[OSD([sQuery(id+"F24.wireOp",EDGE,"E42.MirrorCS"),sQuery(id+"F24.wireOp",EDGE,"E43.MirrorCS")])]});
            var Q11;
            Q11=makeQuery(id+"F25.opExtrude","SWEPT_EDGE",EDGE,{"disambiguationData":[OSD([sQuery(id+"F0.wireOp",EDGE,"E1.0"),sQuery(id+"F24.wireOp",EDGE,"E42.MirrorCS")])]});
            var Q12;
            Q12=makeQuery(id+"F25.opExtrude","SWEPT_EDGE",EDGE,{"disambiguationData":[OSD([sQuery(id+"F0.wireOp",EDGE,"E1.0"),sQuery(id+"F24.wireOp",EDGE,"E41.MirrorCS")])]});
            var Q13;
            Q13=makeQuery(id+"F25.opExtrude","SWEPT_EDGE",EDGE,{"disambiguationData":[OSD([sQuery(id+"F24.wireOp",EDGE,"E37.MirrorCS"),sQuery(id+"F24.wireOp",EDGE,"E41.MirrorCS")])]});
            var Q14;
            Q14=makeQuery(id+"F25.opExtrude","SWEPT_EDGE",EDGE,{"disambiguationData":[OSD([sQuery(id+"F24.wireOp",EDGE,"E36.MirrorCS"),sQuery(id+"F24.wireOp",EDGE,"E37.MirrorCS")])]});
            var Q15;
            Q15=makeQuery(id+"F25.opExtrude","SWEPT_EDGE",EDGE,{"disambiguationData":[OSD([sQuery(id+"F0.wireOp",EDGE,"E1.0"),sQuery(id+"F24.wireOp",EDGE,"E36.MirrorCS")])]});
            fillet(context, id + "F26", {"entities" : qUnion([Q0, Q1, Q2, Q3, Q4, Q5, Q6, Q7, Q8, Q9, Q10, Q11, Q12, Q13, Q14, Q15]), "radius" : 5 * mm, "tangentPropagation" : true, "allowEdgeOverflow" : false});
        }
        {
            var Q0;
            Q0=makeQuery(id+"F25.opExtrude","SWEPT_EDGE",EDGE,{"disambiguationData":[OSD([sQuery(id+"F24.wireOp",EDGE,"E38.MirrorCS"),sQuery(id+"F24.wireOp",EDGE,"E40.MirrorCS")])]});
            var Q1;
            Q1=makeQuery(id+"F25.opExtrude","SWEPT_EDGE",EDGE,{"disambiguationData":[OSD([sQuery(id+"F24.wireOp",EDGE,"E44.MirrorCS"),sQuery(id+"F24.wireOp",EDGE,"E46.MirrorCS")])]});
            var Q2;
            Q2=makeQuery(id+"F25.opExtrude","SWEPT_EDGE",EDGE,{"disambiguationData":[OSD([sQuery(id+"F24.wireOp",EDGE,"E44.MirrorCS"),sQuery(id+"F24.wireOp",EDGE,"E45.MirrorCS")])]});
            var Q3;
            Q3=makeQuery(id+"F25.opExtrude","SWEPT_EDGE",EDGE,{"disambiguationData":[OSD([sQuery(id+"F24.wireOp",EDGE,"E38.MirrorCS"),sQuery(id+"F24.wireOp",EDGE,"E39.MirrorCS")])]});
            var Q4;
            Q4=makeQuery(id+"F25.opExtrude","SWEPT_EDGE",EDGE,{"disambiguationData":[OSD([sQuery(id+"F24.wireOp",EDGE,"E31.top"),sQuery(id+"F24.wireOp",EDGE,"E31.left")])]});
            var Q5;
            Q5=makeQuery(id+"F25.opExtrude","SWEPT_EDGE",EDGE,{"disambiguationData":[OSD([sQuery(id+"F24.wireOp",EDGE,"E34.top"),sQuery(id+"F24.wireOp",EDGE,"E34.left")])]});
            var Q6;
            Q6=makeQuery(id+"F25.opExtrude","SWEPT_EDGE",EDGE,{"disambiguationData":[OSD([sQuery(id+"F24.wireOp",EDGE,"E31.top"),sQuery(id+"F24.wireOp",EDGE,"E31.right")])]});
            var Q7;
            Q7=makeQuery(id+"F25.opExtrude","SWEPT_EDGE",EDGE,{"disambiguationData":[OSD([sQuery(id+"F24.wireOp",EDGE,"E34.top"),sQuery(id+"F24.wireOp",EDGE,"E34.right")])]});
            var Q8;
            Q8=makeQuery(id+"F25.opExtrude","SWEPT_EDGE",EDGE,{"disambiguationData":[OSD([sQuery(id+"F24.wireOp",EDGE,"E30.bottom"),sQuery(id+"F24.wireOp",EDGE,"E31.bottom"),sQuery(id+"F24.wireOp",EDGE,"E31.right")])]});
            var Q9;
            Q9=makeQuery(id+"F25.opExtrude","SWEPT_EDGE",EDGE,{"disambiguationData":[OSD([sQuery(id+"F24.wireOp",EDGE,"E30.bottom"),sQuery(id+"F24.wireOp",EDGE,"E31.bottom"),sQuery(id+"F24.wireOp",EDGE,"E31.left")])]});
            var Q10;
            Q10=makeQuery(id+"F25.opExtrude","SWEPT_EDGE",EDGE,{"disambiguationData":[OSD([sQuery(id+"F24.wireOp",EDGE,"E33.bottom"),sQuery(id+"F24.wireOp",EDGE,"E34.bottom"),sQuery(id+"F24.wireOp",EDGE,"E34.right")])]});
            var Q11;
            Q11=makeQuery(id+"F25.opExtrude","SWEPT_EDGE",EDGE,{"disambiguationData":[OSD([sQuery(id+"F24.wireOp",EDGE,"E33.bottom"),sQuery(id+"F24.wireOp",EDGE,"E34.bottom"),sQuery(id+"F24.wireOp",EDGE,"E34.left")])]});
            var Q12;
            Q12=makeQuery(id+"F25.opExtrude","SWEPT_EDGE",EDGE,{"disambiguationData":[OSD([sQuery(id+"F0.wireOp",EDGE,"E1.0"),sQuery(id+"F24.wireOp",EDGE,"E45.MirrorCS")])]});
            var Q13;
            Q13=makeQuery(id+"F25.opExtrude","SWEPT_EDGE",EDGE,{"disambiguationData":[OSD([sQuery(id+"F0.wireOp",EDGE,"E1.0"),sQuery(id+"F24.wireOp",EDGE,"E46.MirrorCS")])]});
            var Q14;
            Q14=makeQuery(id+"F25.opExtrude","SWEPT_EDGE",EDGE,{"disambiguationData":[OSD([sQuery(id+"F0.wireOp",EDGE,"E1.0"),sQuery(id+"F24.wireOp",EDGE,"E40.MirrorCS")])]});
            var Q15;
            Q15=makeQuery(id+"F25.opExtrude","SWEPT_EDGE",EDGE,{"disambiguationData":[OSD([sQuery(id+"F0.wireOp",EDGE,"E1.0"),sQuery(id+"F24.wireOp",EDGE,"E39.MirrorCS")])]});
            fillet(context, id + "F27", {"entities" : qUnion([Q0, Q1, Q2, Q3, Q4, Q5, Q6, Q7, Q8, Q9, Q10, Q11, Q12, Q13, Q14, Q15]), "radius" : 5 * mm, "tangentPropagation" : true, "allowEdgeOverflow" : false});
        }
    });
